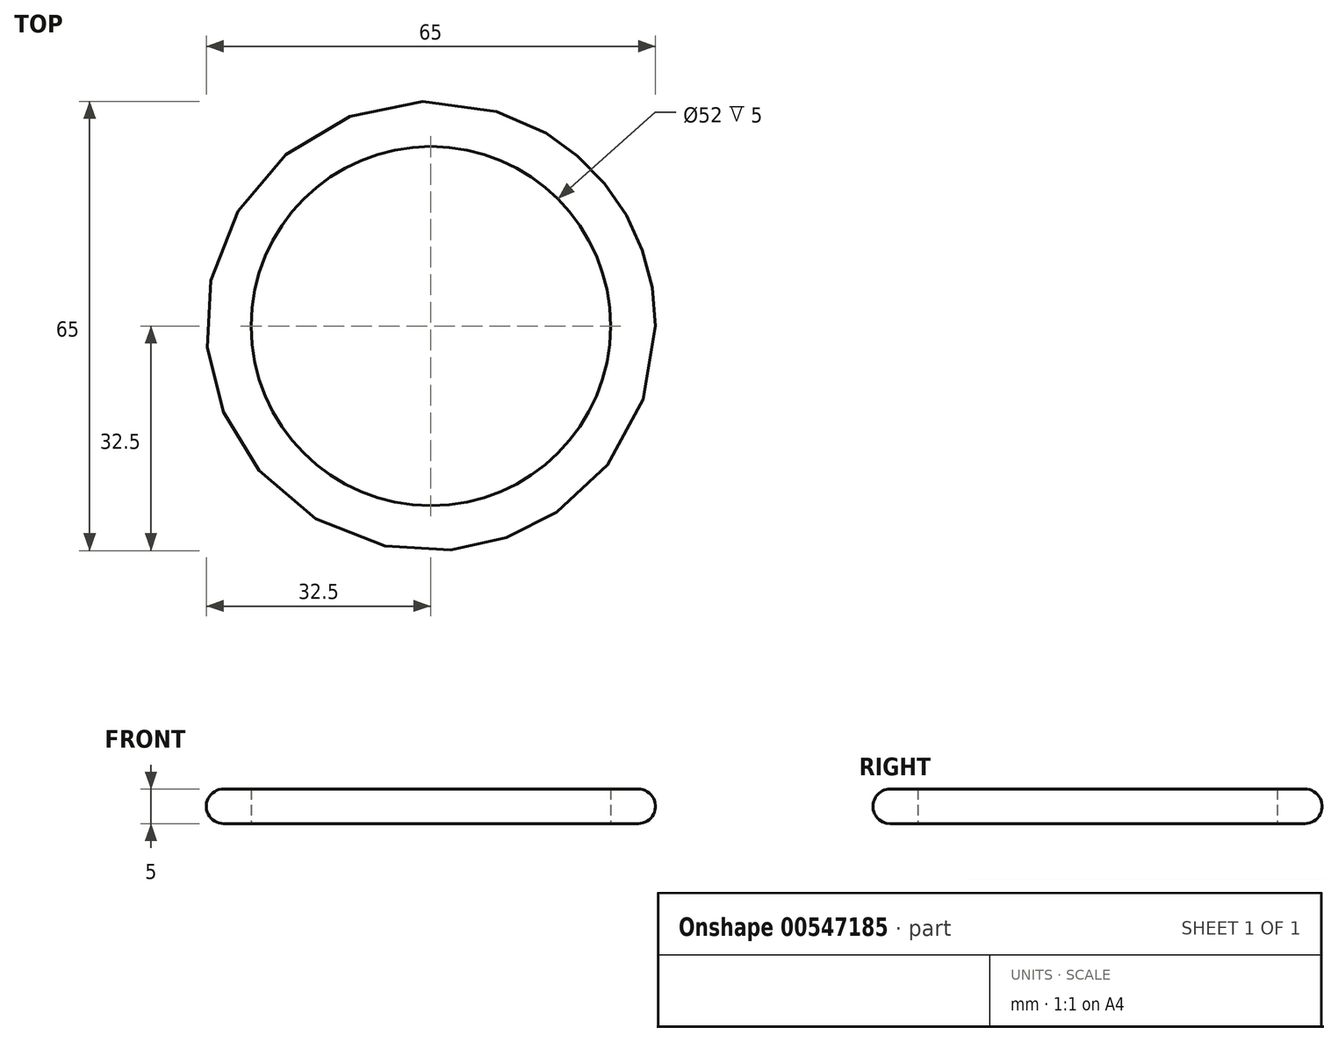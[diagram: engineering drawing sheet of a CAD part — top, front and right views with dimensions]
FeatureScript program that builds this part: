
annotation { "Feature Type Name" : "Feature", "Feature Type Description" : "" }
export const myFeature = defineFeature(function(context is Context, id is Id, definition is map)
    precondition{}
    {
        {
            var Q0;
            Q0=qCreatedBy(makeId("Top.planeOp"),FACE);
            var sketch = newSketch(context, id + "F0", { "sketchPlane" : qUnion([Q0])});
            skCircle(sketch, "E0", {"center": v(0, 0) * mm, "radius": 26 * mm});
            skCircle(sketch, "E1", {"center": v(0, 0) * mm, "radius": 32.5 * mm});
            skSolve(sketch);
        }
        {
            var Q0;
            Q0 = qSketchRegion(id + "F0", true);
            extrude(context, id + "F1", {"entities" : qUnion([Q0]), "depth" : 5 * mm, "offsetDistance" : 25 * mm});
        }
        {
            var Q0;
            Q0=makeQuery(id+"F1.opExtrude","SWEPT_FACE",FACE,{"disambiguationData":[OSD([sQuery(id+"F0.wireOp",EDGE,"E1")])]});
            fillet(context, id + "F2", {"entities" : qUnion([Q0]), "radius" : 2.5 * mm, "tangentPropagation" : true, "allowEdgeOverflow" : false});
        }
    });
